# Revit family: All-Lite Louver_EFJ-937_R15
name_source: partatom
category: Mechanical Equipment
revit_build: Autodesk Revit 2017 (Build: 20160225_1515(x64)
units: mm (PartAtom-declared; Revit-internal decimal feet)

## family parameters
Always vertical = Yes
Cut with Voids When Loaded = No
Host = Wall
Part Type = Normal
Room Calculation Point = No
Round Connector Dimension = Use Diameter
Shared = No

## types (1)
- EFJ-937
    04 CSI = 08 91 00
    95 CSI = 10200
    Air Volume Delivered @ Beginning Point of Water Penetration = Above 10775 cfm
    Assembly Code = B2010300
    Blade Width = 3' - 10"
    Blades = Front: 37° x 0.081'' thick horizontal J style Rear: 0.06'' thick vertical chevron
    Cut Sheet = http://www.alllite.com
    Default Height = 4' - 0"
    Description = The EFJ-937 dual-module louver is engineered and tested
to withstand extreme loads, debris impact, and cyclic
fatigue associated with the severe weather effects of hurricanes.
The front (exterior) side of the louver features horizontal
J-style blades for a pleasing architectural appearance. The
interior side features vertical chevron blades which provide
superior resistance to wind-driven rain. Both installation options
for the EFJ-937 feature minimal required hardware. The
EFJ-937 is AMCA 540 and 550 listed, making it ideally suited for
use in hurricane-prone and wind-borne debris regions per the
International Building Code.
    Design Load = 130 psf
    Frame = 9'' deep x 0.125'' thick channel
    Free Area = [48'' x 48'' unit] : 8.6 ft² 53.9%
    Free Area Velocity @ Beginning Point of Water Penetration = Above 1250 fpm
    Height = 4' - 0"
    Height Control = 4' - 0"
    Louver = Aluminum
    Louver Count = 11
    Manufacturer = Pottorff
    Max Height = 10' - 0"
    Max Width = 5' - 0"
    Maximum Size - Multiple Section = Unlimited width x 120''
    Maximum Size - Single Section = 60'' x 120''
    Min Height = 1' - 0"
    Min Width = 1' - 0"
    Minimum Size = 12'' x 12''
    Model = EFJ-937
    Mullion = Visible
    Omni Class Code = 23-60 11 17
    Omni Class Title = Exterior Louvers & Grilles
    Pressure Loss @ Beginning Point of Water Penetration = 0.48 in. wg.
    Product URL = http://www.alllite.com
    Screen = 1/2'' x .063'' expanded and flattened aluminum
    Specifications = javascript://EFJ-937 CSI Specification
    URL = http://alllite.com
    Velocity @ 0.15 in. wg. Pressure Loss = 705 fpm
    Vertical Blade Height = 3' - 10"
    Vertical Louver Array = 33
    Warranty = http://www.alllite.com
    Width = 4' - 0"
    Width Control = 4' - 0"

## geometry (parser evidence)
native form markers: Blend x6, Sweep x9
no freeform markers — native parametric forms only
